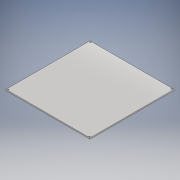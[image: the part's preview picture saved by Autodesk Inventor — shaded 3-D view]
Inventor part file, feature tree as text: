
AUTODESK INVENTOR PART (.ipt)
format: ipt  version: 2017 (Build 210142000, 142)  size: 108,032 bytes
history: native  units: mm
features: extrude x2, sketch x2, projected_geometry x1
ambient origin geometry x8: Origin, YZ Plane, XZ Plane, XY Plane, X Axis, Y Axis, Z Axis, Center Point
bodies: Solid1 (feature_tree)
feature tree (5):
  extrude  "Extrusion1"  Depth=3.0mm TaperAngle=0.0deg
  extrude  "Extrusion2"  Depth=3.0mm
  sketch  "Sketch1"  dims[d0=213.0mm d1=3.0mm d2=0.0mm]
  sketch  "Sketch2"  dims[d3=3.0mm d4=2.0mm d5=1.0mm d6=3.0mm d7=0.0mm]
  projected_geometry  "Projected Loop1"
